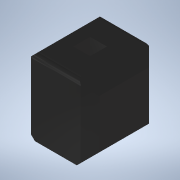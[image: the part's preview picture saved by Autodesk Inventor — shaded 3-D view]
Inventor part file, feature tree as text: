
AUTODESK INVENTOR PART (.ipt)
format: ipt  version: 2021 (Build 250183000, 183)  size: 181,248 bytes
history: native  units: mm
features: extrude x1, sketch x1, imported_body x1
ambient origin geometry x8: Origin, YZ Plane, XZ Plane, XY Plane, X Axis, Y Axis, Z Axis, Center Point
bodies: Solid1 (feature_tree)
feature tree (3):
  extrude  "Extrusion1"  [1 undecoded]
  sketch  "Sketch1"  dims[d0=12.7mm d1=0.0mm]
  imported_body  "Base1"
note: 1 required parameter value undecoded (feature->parameter linkage not recoverable at this tier; creation-order binding heuristic only, values carry confidence <= 0.55)
